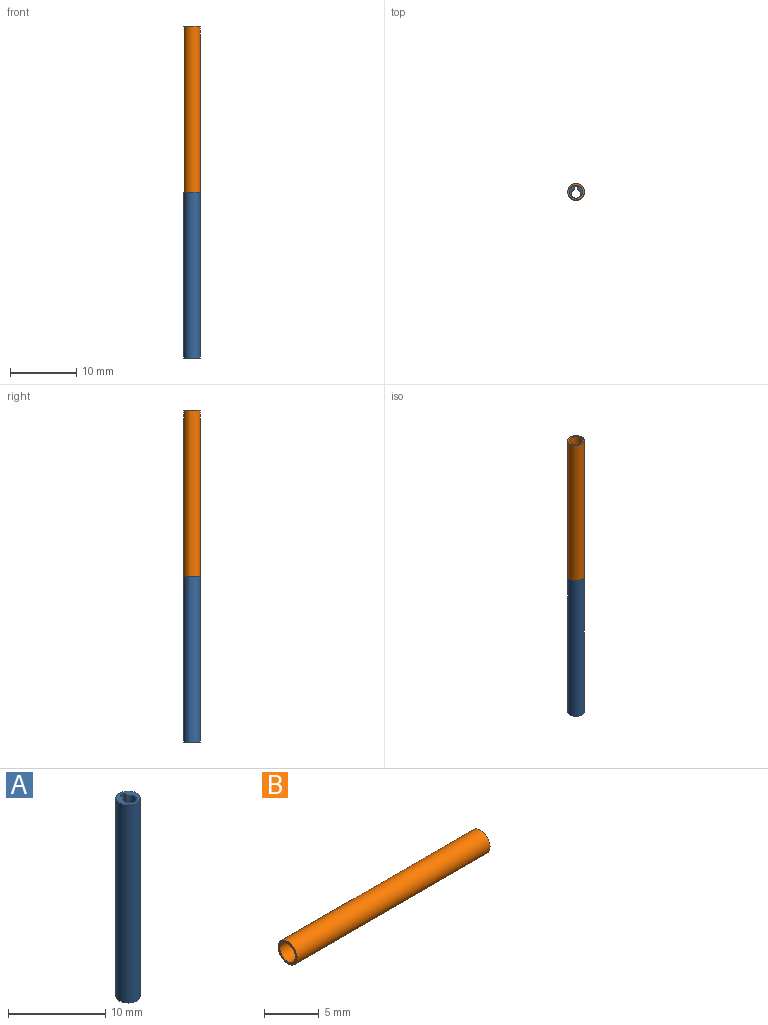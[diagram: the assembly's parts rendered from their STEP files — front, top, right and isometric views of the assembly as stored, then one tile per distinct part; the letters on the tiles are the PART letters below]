
ASSEMBLY  parts=2 mates=1
PART A: 5 faces, bbox 2.5x2.5x25 mm
  f0: cylinder r=0.3mm len=25mm, axis (0,0,-1), area 36.5mm2, adj f2,f3,f4
  f1: cylinder r=1.25mm len=25mm, axis (0,0,-1), area 196.3mm2, adj f3,f4
  f2: cylinder r=0.7mm len=25mm, axis (0,0,-1), area 100.1mm2, adj f0,f3,f4
  f3: plane 2.5x2.5mm, normal (0,0,1), area 3.1mm2, adj f0,f1,f2
  f4: plane 2.5x2.5mm, normal (0,0,-1), area 3.1mm2, adj f0,f1,f2
PART B: 4 faces, bbox 25x2.5x2.5 mm
  f0: cylinder r=1mm len=25mm, axis (-1,0,0), area 157.1mm2, adj f2,f3
  f1: cylinder r=1.25mm len=25mm, axis (-1,0,0), area 196.3mm2, adj f2,f3
  f2: plane 2.5x2.5mm, normal (1,0,0), area 1.8mm2, adj f0,f1
  f3: plane 2.5x2.5mm, normal (-1,0,0), area 1.8mm2, adj f0,f1
PLACE A t=(-6.73,2.64,-2.72)mm
PLACE B rot(axis=(0,-1,0),90deg) t=(-6.73,2.64,22.28)mm
MATE fastened B.f0 <-> A.f1  axis (0,0,-1) through (-6.73,2.64,22.28)mm
